# Revit family: Haworth_Kennedee_Sectional_ArmlessWithBench
name_source: partatom
category: Furniture
revit_build: Autodesk Revit 2018 (Build: 20170223_1515(x64)
units: mm (PartAtom-declared; Revit-internal decimal feet)

## family parameters
Always vertical = Yes
Cut with Voids When Loaded = No
OmniClass Number = 23.40.70.14.64.21
OmniClass Title = Systems Furniture
Room Calculation Point = No
Shared = No
Work Plane-Based = No

## types (3) — shared parameters
Assembly Code = E2020200
Base Finish = Haworth _ Paint _ Metallic Gunmetal
Description = Haworth Kennedee Sectional Armless With Bench
Manufacturer = Haworth
Model = HCPF-KEL
Revision Number = 4
Size = Verify Final Dim. w/ Haworth
URL = http://www.haworth.com
URL - Product = http://www.haworth.com
Warranty = http://www.haworth.com

## per-type parameters (varying)
| type | Actual Width | Middle Seat Control | One Seat | Three Seats | Two Seats |
| HCPF-KEL - Two Seats | 92 195/256" | Yes | No | No | Yes |
| HCPF-KEL - One Seat | 57 67/256" | No | Yes | No | No |
| HCPF-KEL - Three Seats | 128 67/256" | Yes | No | Yes | No |

## geometry (parser evidence)
native form markers: Sweep x14
no freeform markers — native parametric forms only
